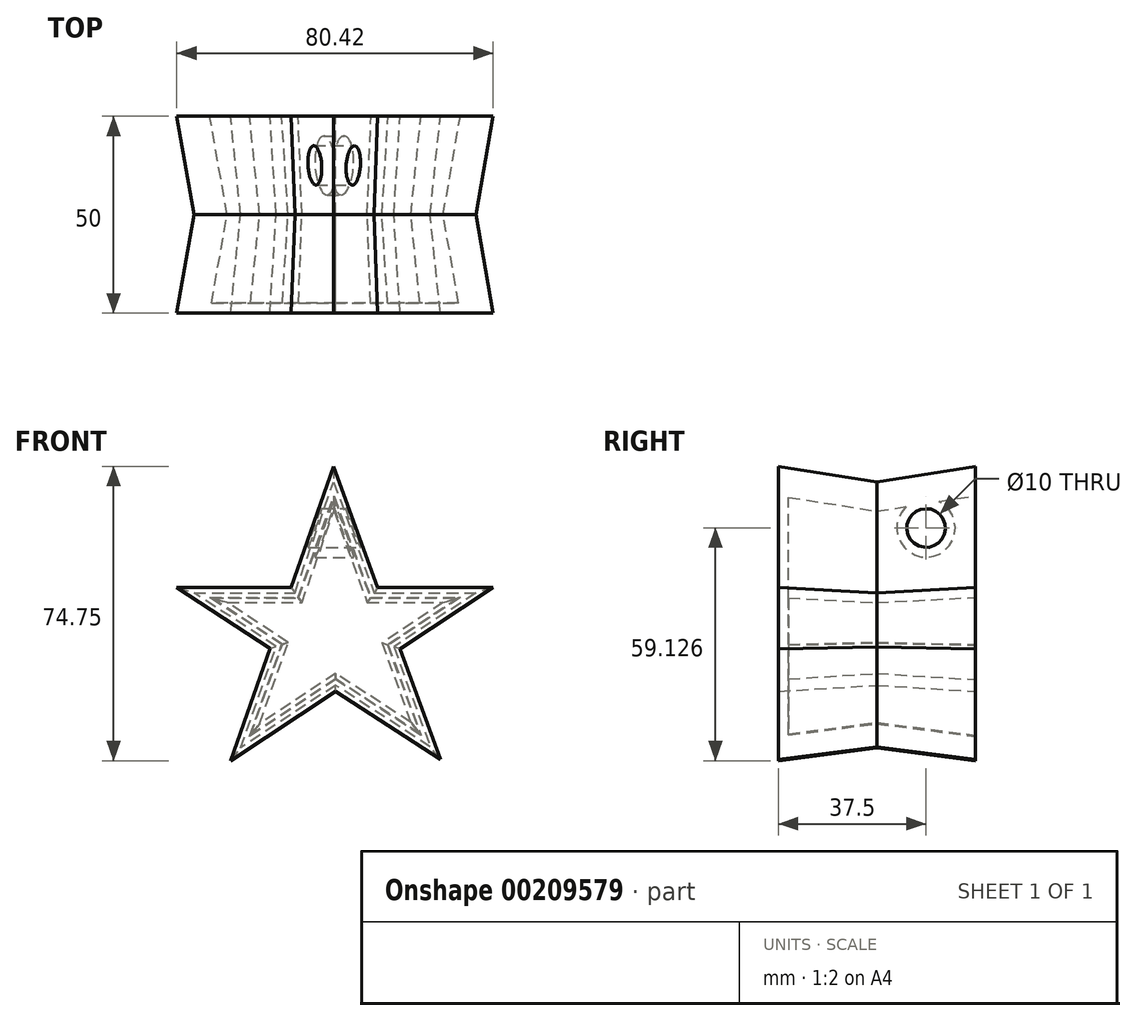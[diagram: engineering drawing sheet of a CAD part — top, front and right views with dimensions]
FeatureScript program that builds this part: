
annotation { "Feature Type Name" : "Feature", "Feature Type Description" : "" }
export const myFeature = defineFeature(function(context is Context, id is Id, definition is map)
    precondition{}
    {
        {
            var Q0;
            Q0=qCreatedBy(makeId("Front.planeOp"),FACE);
            var sketch = newSketch(context, id + "F0", { "sketchPlane" : qUnion([Q0])});
            skLineSegment(sketch, "E0", {"start": v(-48.18, -0.3) * mm, "end": v(-24.52, 67.33) * mm});
            skLineSegment(sketch, "E1", {"start": v(-24.52, 67.33) * mm, "end": v(0, 0) * mm});
            skLineSegment(sketch, "E2", {"start": v(0, 0) * mm, "end": v(-60.01, 39.14) * mm});
            skLineSegment(sketch, "E3", {"start": v(-60.01, 39.14) * mm, "end": v(11.64, 39.14) * mm});
            skLineSegment(sketch, "E4", {"start": v(11.64, 39.14) * mm, "end": v(-48.18, -0.3) * mm});
            skSolve(sketch);
        }
        {
            var Q0;
            Q0 = qSketchRegion(id + "F0", true);
            extrude(context, id + "F1", {"entities" : qUnion([Q0]), "depth" : 25 * mm, "hasDraft" : true, "draftAngle" : 3 * degree, "hasSecondDirection" : true, "secondDirectionOppositeDirection" : true, "secondDirectionDepth" : 25 * mm, "hasSecondDirectionDraft" : true, "secondDirectionDraftAngle" : 3 * degree});
        }
        {
            var Q0;
            Q0=qCreatedBy(makeId("Right.planeOp"),FACE);
            var sketch = newSketch(context, id + "F2", { "sketchPlane" : qUnion([Q0])});
            skCircle(sketch, "E5", {"center": v(12.5, 55.6) * mm, "radius": 5 * mm});
            skPoint(sketch, "E6", {"position": v(12.5, 69.27) * mm});
            skPoint(sketch, "E6.positionSnap0", {"position": v(12.5, 69.27) * mm});
            skPoint(sketch, "E7", {"position": v(0, 55.6) * mm});
            skSolve(sketch);
        }
        {
            var Q0;
            Q0 = qSketchRegion(id + "F2", true);
            extrude(context, id + "F3", {"entities" : qUnion([Q0]), "operationType" : NewBodyOperationType.REMOVE, "endBound" : BoundingType.THROUGH_ALL, "oppositeDirection" : true, "depth" : 40 * mm});
        }
        {
            var Q0;
            Q0=makeQuery(id+"F1.opExtrude","CAP_FACE",FACE,{"disambiguationData":[OSD([sQuery(id+"F0.wireOp",EDGE,"E0"),sQuery(id+"F0.wireOp",EDGE,"E1"),sQuery(id+"F0.wireOp",EDGE,"E2"),sQuery(id+"F0.wireOp",EDGE,"E3"),sQuery(id+"F0.wireOp",EDGE,"E4")])],"isStart":true});
            shell(context, id + "F4", {"entities" : qUnion([Q0]), "thickness" : 2.5 * mm});
        }
    });
